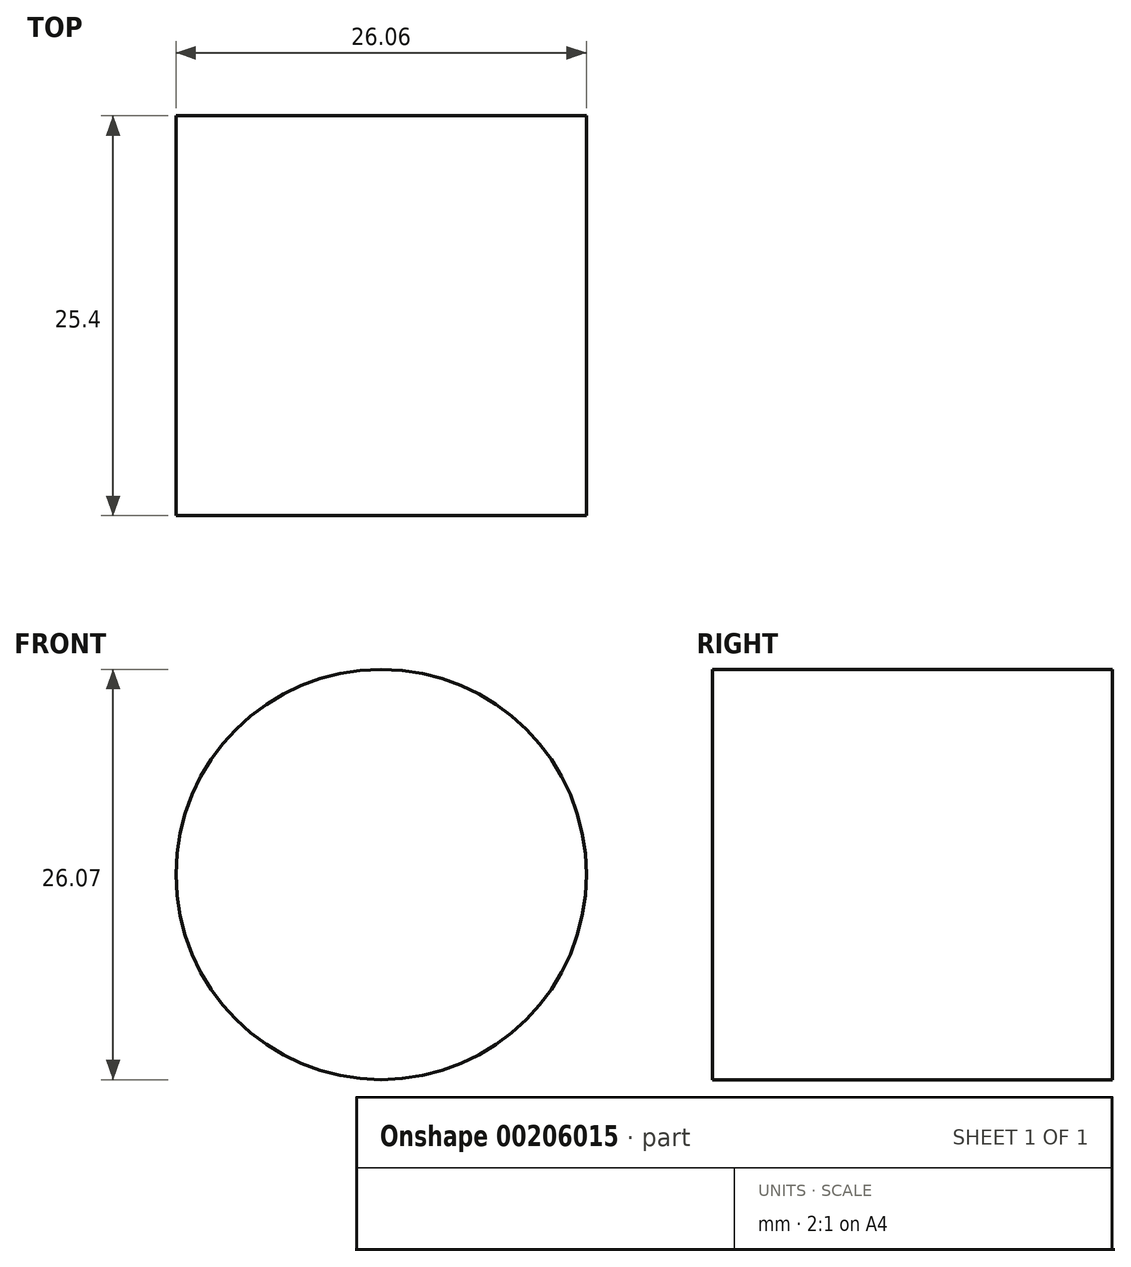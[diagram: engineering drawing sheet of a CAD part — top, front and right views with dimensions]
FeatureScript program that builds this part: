
annotation { "Feature Type Name" : "Feature", "Feature Type Description" : "" }
export const myFeature = defineFeature(function(context is Context, id is Id, definition is map)
    precondition{}
    {
        {
            var Q0;
            Q0=qCreatedBy(makeId("Front.planeOp"),FACE);
            var sketch = newSketch(context, id + "F0", { "sketchPlane" : qUnion([Q0])});
            skLineSegment(sketch, "E0.bottom", {"start": v(-50.67, 45.66) * mm, "end": v(31.8, 45.66) * mm});
            skLineSegment(sketch, "E0.top", {"start": v(-50.67, -9.52) * mm, "end": v(31.8, -9.52) * mm});
            skLineSegment(sketch, "E0.left", {"start": v(-50.67, 45.66) * mm, "end": v(-50.67, -9.52) * mm});
            skLineSegment(sketch, "E0.right", {"start": v(31.8, 45.66) * mm, "end": v(31.8, -9.52) * mm});
            skSolve(sketch);
        }
        {
            var Q0;
            Q0=makeQuery(id+"F0.imprint","IMPRINT",FACE,{"disambiguationData":[TD([[makeQuery(id+"F0.imprint","IMPRINT",EDGE,{"derivedFrom":sQuery(id+"F0.wireOp",EDGE,"E0.bottom")}),-1.0]])]});
            extrude(context, id + "F1", {"entities" : qUnion([Q0]), "endBound" : BoundingType.SYMMETRIC, "depth" : 25.4 * mm});
        }
        {
            var Q0;
            Q0=makeQuery(id+"F1.opExtrude","CAP_FACE",FACE,{"disambiguationData":[OSD([sQuery(id+"F0.wireOp",EDGE,"E0.bottom"),sQuery(id+"F0.wireOp",EDGE,"E0.top"),sQuery(id+"F0.wireOp",EDGE,"E0.left"),sQuery(id+"F0.wireOp",EDGE,"E0.right")])],"isStart":false});
            var sketch = newSketch(context, id + "F2", { "sketchPlane" : qUnion([Q0])});
            skCircle(sketch, "E1", {"center": v(-11.54, 22.07) * mm, "radius": 13.03 * mm});
            skSolve(sketch);
        }
        {
            var Q0;
            Q0=makeQuery(id+"F2.imprint","IMPRINT",FACE,{"disambiguationData":[TD([[makeQuery(id+"F2.imprint","IMPRINT",EDGE,{"derivedFrom":sQuery(id+"F2.wireOp",EDGE,"E1")}),1.0]])]});
            extrude(context, id + "F3", {"entities" : qUnion([Q0]), "operationType" : NewBodyOperationType.INTERSECT, "oppositeDirection" : true, "depth" : 25.4 * mm});
        }
    });
